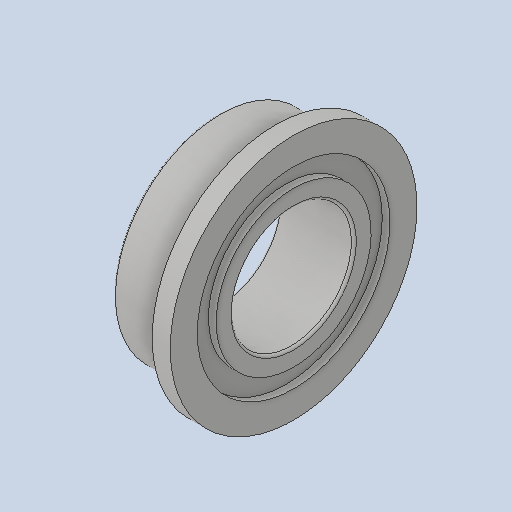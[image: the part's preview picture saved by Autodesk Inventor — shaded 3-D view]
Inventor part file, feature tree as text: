
AUTODESK INVENTOR PART (.ipt)
format: ipt  version: 2022 (Build 260153000, 153)  size: 212,480 bytes
history: native  units: mm
features: other x7, revolve x1, sketch x1
ambient origin geometry x8: Origin, YZ Plane, XZ Plane, XY Plane, X Axis, Y Axis, Z Axis, Center Point
bodies: Solid1 (feature_tree)
feature tree (9):
  revolve  "Revolution1"  [1 undecoded]
  other  "to_housing_XY"
  other  "to_housing_YZ"
  other  "to_housing_ZX"
  other  "to_housing_X"
  other  "to_housing_Y"
  other  "to_housing_Z"
  other  "to_housing_Center"
  sketch  "Sketch_1"  dims[d0=360.0deg d1=0.0mm]
note: 1 required parameter value undecoded (feature->parameter linkage not recoverable at this tier; creation-order binding heuristic only, values carry confidence <= 0.55)
